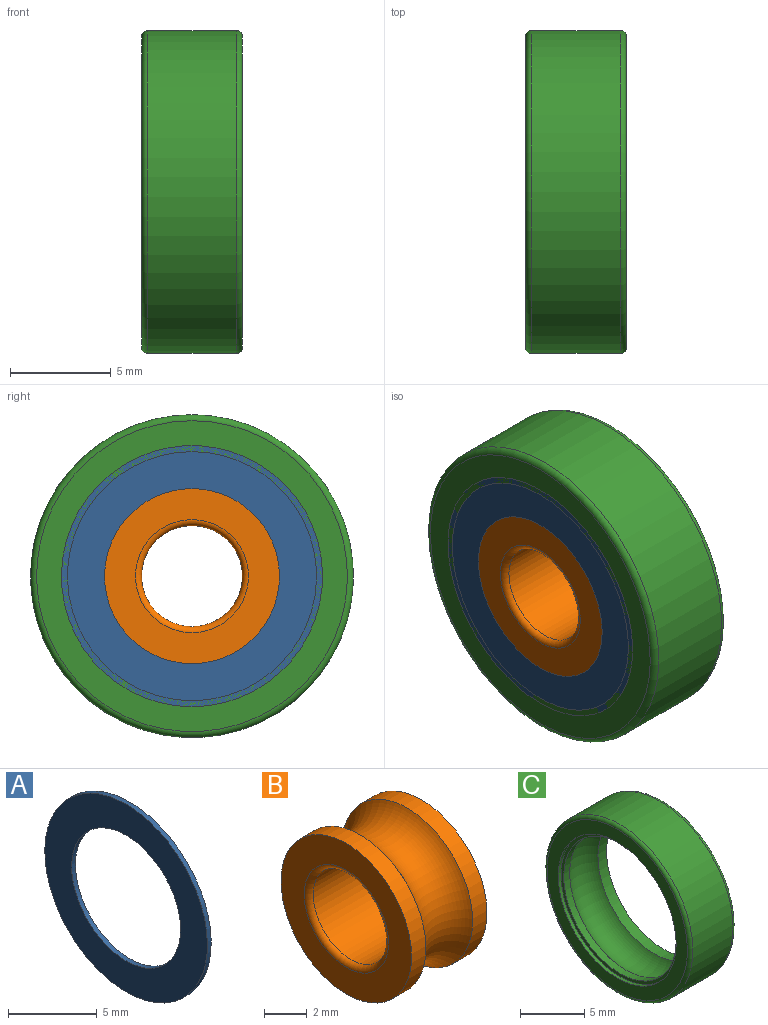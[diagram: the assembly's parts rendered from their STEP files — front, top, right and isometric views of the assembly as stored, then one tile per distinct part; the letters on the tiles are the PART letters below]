
ASSEMBLY  parts=3 mates=2
PART A: 4 faces, bbox 0.3x12.9x12.9 mm
  f0: cylinder r=6.47mm len=12.93mm, axis (1,0,0), area 12.2mm2, adj f1,f3
  f1: plane 12.93x12.93mm, normal (-1,0,0), area 72.4mm2, adj f0,f2
  f2: cylinder r=4.33mm len=8.67mm, axis (1,0,0), area 8.2mm2, adj f1,f3
  f3: plane 12.93x12.93mm, normal (1,0,0), area 72.4mm2, adj f0,f2
PART B: 8 faces, bbox 5x11.4x11.4 mm
  f0: cylinder r=4.33mm len=8.67mm, axis (1,0,0), area 25.9mm2, adj f1,f7
  f1: plane 8.67x8.67mm, normal (-1,0,0), area 34.4mm2, adj f0,f2
  f2: torus R=2.8mm, axis (1,0,0), area 7.7mm2, adj f1,f3
  f3: cylinder r=2.5mm len=5mm, axis (1,0,0), area 69.1mm2, adj f2,f4
  f4: torus R=2.8mm, axis (1,0,0), area 7.7mm2, adj f3,f5
  f5: plane 8.67x8.67mm, normal (1,0,0), area 34.4mm2, adj f4,f6
  f6: cylinder r=4.33mm len=8.67mm, axis (1,0,0), area 25.9mm2, adj f5,f7
  f7: torus R=5.25mm, axis (1,0,0), area 88mm2, adj f0,f6
PART C: 10 faces, bbox 5x17.3x17.3 mm
  f0: torus R=7.7mm, axis (1,0,0), area 23.4mm2, adj f1,f9
  f1: plane 15.4x15.4mm, normal (-1,0,0), area 54.9mm2, adj f0,f2
  f2: cylinder r=6.47mm len=12.93mm, axis (1,0,0), area 12.2mm2, adj f1,f3
  f3: plane 12.93x12.93mm, normal (-1,0,0), area 11.9mm2, adj f2,f4
  f4: cylinder r=6.17mm len=12.33mm, axis (1,0,0), area 25.2mm2, adj f3,f5
  f5: torus R=5.25mm, axis (1,0,0), area 158.1mm2, adj f4,f6
  f6: cylinder r=6.17mm len=12.33mm, axis (1,0,0), area 36.8mm2, adj f5,f7
  f7: plane 15.4x15.4mm, normal (1,0,0), area 66.8mm2, adj f6,f8
  f8: torus R=7.7mm, axis (1,0,0), area 23.4mm2, adj f7,f9
  f9: cylinder r=8mm len=16mm, axis (1,0,0), area 221.2mm2, adj f0,f8
PLACE A t=(5,0,0)mm
PLACE B t=(5,0,0)mm
PLACE C rot(axis=(0,1,0),180deg) t=(10,0,0)mm
MATE fastened A.f0 <-> C.f0  axis (-1,0,0) through (5,0,0)mm
MATE fastened B.f0 <-> C.f0  axis (1,0,0) through (10,0,0)mm
